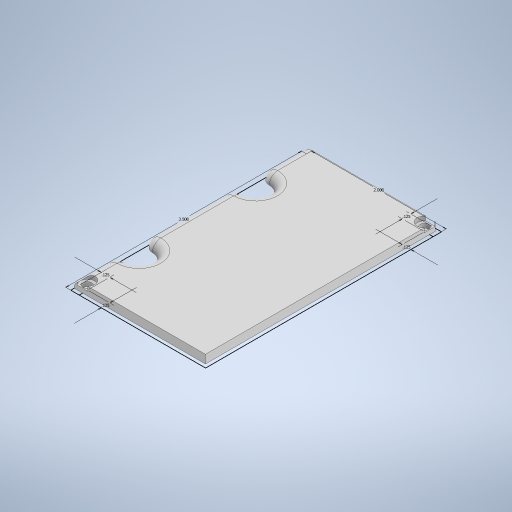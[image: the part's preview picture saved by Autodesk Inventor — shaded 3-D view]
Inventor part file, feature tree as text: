
AUTODESK INVENTOR PART (.ipt)
format: ipt  version: 2024.1 (Build 281209000, 209)  size: 318,464 bytes
history: native  units: in
note: dims shown in document units (in); Inventor stores cm internally (conversion verified against a paired STEP export)
features: extrude x2, fillet x2, hole x1, sketch x1
ambient origin geometry x8: Origin, YZ Plane, XZ Plane, XY Plane, X Axis, Y Axis, Z Axis, Center Point
bodies: Solid1 (feature_tree)
feature tree (6):
  extrude  "Extrusion1"  Depth=0.125in
  hole  "Hole2"  [1 undecoded]
  fillet  "Fillet1"  Radius=0.125in
  extrude  "Extrusion2"  Depth=0.125in
  fillet  "Fillet2"  Radius=0.125in
  sketch  "Sketch3"  dims[d0=2.0in d1=3.5in d2=0.125in d3=0.125in d4=0.125in d5=0.125in d6=0.125in d7=0.0in d15=0.125in d16=0.125in d17=0.125in d18=0.125in d19=0.129in d20=0.75in d21=0.219in d22=0.0625in d23=0.5635in d24=0.25in d25=0.0in d26=0.125in d27=0.05in d28=0.05in d29=0.05in d30=0.888in d31=0.888in d32=0.125in d33=0.4in d34=0.125in d35=0.4in d36=1.0in d37=0.0in d38=0.125in]
note: 1 required parameter value undecoded (feature->parameter linkage not recoverable at this tier; creation-order binding heuristic only, values carry confidence <= 0.55)
